# Revit family: Plumbing Fixture-FloorDrain_Mifab_C1310
name_source: partatom
category: Plumbing Fixtures
revit_build: Autodesk Revit Structure 2013 (Build: 20120221_2030(x64)
units: mm (PartAtom-declared; Revit-internal decimal feet)

## types (6) — shared parameters
Body Height = 1 "
Description = FLOOR ACCESS COVER
Floor Drain Material = Paint - Sherwin Williams Paint - #952C2A - Bellwood Red
Manufacturer = MIFAB
Model = C1310
URL = WWW.MIFAB.COM
zero-valued in all types: Default Elevation, Top Assembly Height, WFU

## per-type parameters (varying)
| type | Cover Diameter | Pipe Diameter | Pipe Radius | Stainer Diameter | Strainer Radius |
| 8" | 10.25 " | 8 " | 4 " | 11.5 " | 5.75 " |
| 2" | 4.5 " | 2 " | 1 " | 5.5 " | 2.75 " |
| 3" | 4.5 " | 3 " | 1.5 " | 5.5 " | 2.75 " |
| 4" | 5.75 " | 4 " | 2 " | 6.75 " | 3.375 " |
| 5" | 7 " | 5 " | 2.5 " | 8 " | 4 " |
| 6" | 8.25 " | 6 " | 3 " | 9.5 " | 4.75 " |

## geometry (parser evidence)
native form markers: Blend x3, Sweep x1
no freeform markers — native parametric forms only
